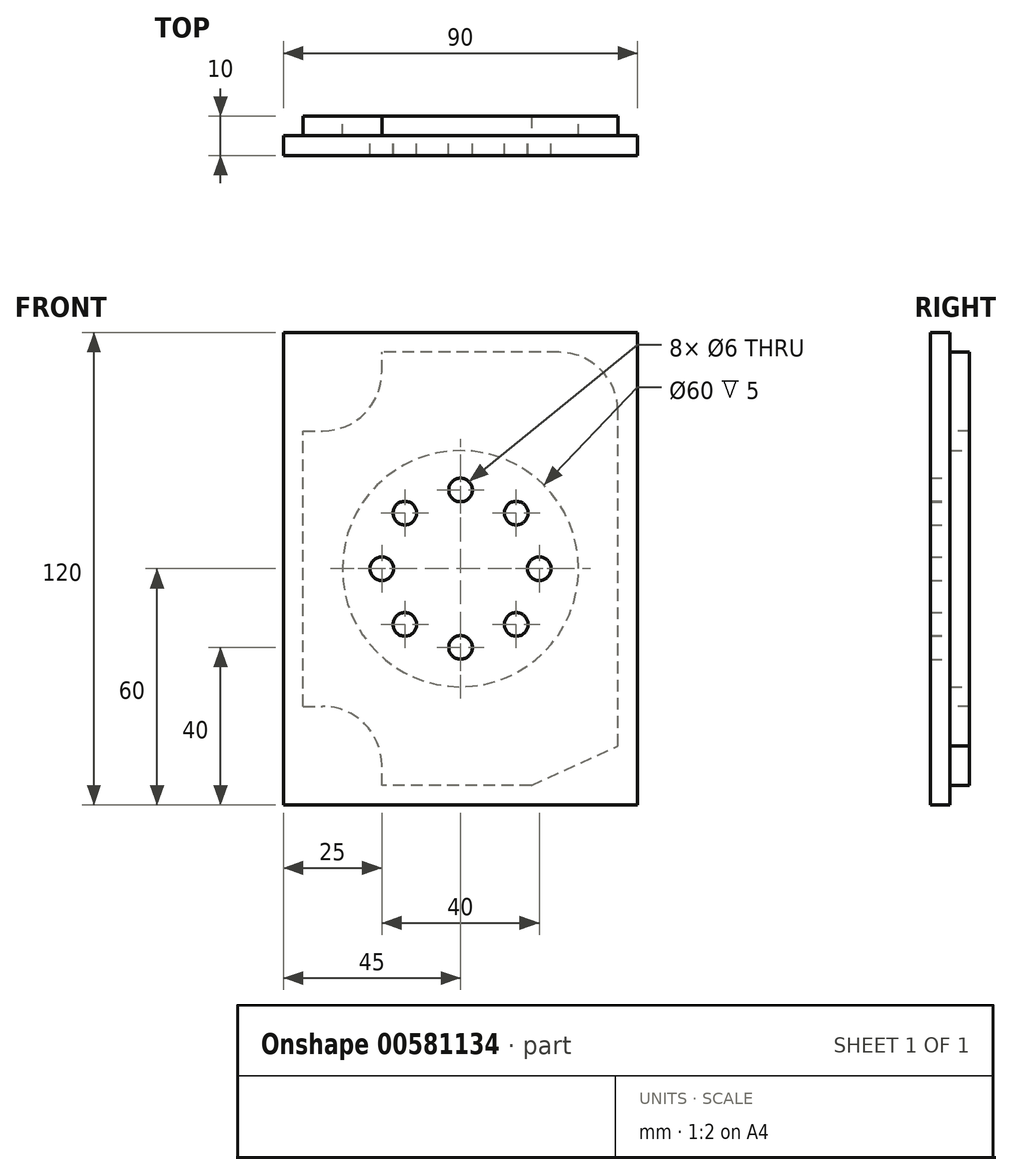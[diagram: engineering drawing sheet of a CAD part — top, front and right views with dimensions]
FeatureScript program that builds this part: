
annotation { "Feature Type Name" : "Feature", "Feature Type Description" : "" }
export const myFeature = defineFeature(function(context is Context, id is Id, definition is map)
    precondition{}
    {
        {
            var Q0;
            Q0=qCreatedBy(makeId("Front.planeOp"),FACE);
            var sketch = newSketch(context, id + "F0", { "sketchPlane" : qUnion([Q0])});
            skLineSegment(sketch, "E0.bottom", {"start": v(45, -60) * mm, "end": v(-45, -60) * mm});
            skLineSegment(sketch, "E0.top", {"start": v(45, 60) * mm, "end": v(-45, 60) * mm});
            skLineSegment(sketch, "E0.left", {"start": v(45, -60) * mm, "end": v(45, 60) * mm});
            skLineSegment(sketch, "E0.right", {"start": v(-45, -60) * mm, "end": v(-45, 60) * mm});
            skLineSegment(sketch, "E1", {"start": v(0, -60) * mm, "end": v(0, 0) * mm, "construction": true});
            skLineSegment(sketch, "E2", {"start": v(0, 0) * mm, "end": v(45, 0) * mm, "construction": true});
            skSolve(sketch);
        }
        {
            var Q0;
            Q0=makeQuery(id+"F0.imprint","IMPRINT",FACE,{"disambiguationData":[TD([[makeQuery(id+"F0.imprint","IMPRINT",EDGE,{"derivedFrom":sQuery(id+"F0.wireOp",EDGE,"E0.bottom")}),-1.0]])]});
            extrude(context, id + "F1", {"entities" : qUnion([Q0]), "depth" : 5 * mm, "offsetDistance" : 25 * mm});
        }
        {
            var Q0;
            Q0=makeQuery(id+"F1.opExtrude","CAP_FACE",FACE,{"disambiguationData":[OSD([sQuery(id+"F0.wireOp",EDGE,"E0.bottom"),sQuery(id+"F0.wireOp",EDGE,"E0.top"),sQuery(id+"F0.wireOp",EDGE,"E0.left"),sQuery(id+"F0.wireOp",EDGE,"E0.right")])],"isStart":true});
            var sketch = newSketch(context, id + "F2", { "sketchPlane" : qUnion([Q0])});
            skLineSegment(sketch, "E3.bottom", {"start": v(-18, -55) * mm, "end": v(20, -55) * mm});
            skLineSegment(sketch, "E3.top", {"start": v(-25, 55) * mm, "end": v(20, 55) * mm});
            skLineSegment(sketch, "E3.left", {"start": v(-40, -45) * mm, "end": v(-40, 40) * mm});
            skLineSegment(sketch, "E3.right", {"start": v(40, -35) * mm, "end": v(40, 35) * mm});
            skPoint(sketch, "E4.visualSharp", {"position": v(-40, 55) * mm});
            skArc(sketch, "E4.filletArc", {"start": v(-25, 55) * mm, "mid": v(-35.6, 50.6) * mm, "end": v(-40, 40) * mm});
            skLineSegment(sketch, "E5", {"start": v(-18, -55) * mm, "end": v(-40, -45) * mm});
            skLineSegment(sketch, "E6", {"start": v(20, -55) * mm, "end": v(20, -50) * mm});
            skLineSegment(sketch, "E7", {"start": v(40, -35) * mm, "end": v(35, -35) * mm});
            skLineSegment(sketch, "E8", {"start": v(40, 35) * mm, "end": v(35, 35) * mm});
            skLineSegment(sketch, "E9", {"start": v(20, 50) * mm, "end": v(20, 55) * mm});
            skArc(sketch, "E10", {"start": v(35, -35) * mm, "mid": v(24.4, -39.4) * mm, "end": v(20, -50) * mm});
            skPoint(sketch, "E11.visualSharp", {"position": v(20, 35) * mm});
            skArc(sketch, "E11.filletArc", {"start": v(20, 50) * mm, "mid": v(24.4, 39.4) * mm, "end": v(35, 35) * mm});
            skSolve(sketch);
        }
        {
            var Q0;
            Q0=makeQuery(id+"F2.imprint","IMPRINT",FACE,{"disambiguationData":[TD([[makeQuery(id+"F2.imprint","IMPRINT",EDGE,{"derivedFrom":sQuery(id+"F2.wireOp",EDGE,"E3.bottom")}),1.0]])]});
            extrude(context, id + "F3", {"entities" : qUnion([Q0]), "operationType" : NewBodyOperationType.ADD, "depth" : 5 * mm, "offsetDistance" : 25 * mm});
        }
        {
            var Q0;
            Q0=makeQuery(id+"F3.opExtrude","CAP_FACE",FACE,{"disambiguationData":[OSD([sQuery(id+"F2.wireOp",EDGE,"E3.bottom"),sQuery(id+"F2.wireOp",EDGE,"E3.top"),sQuery(id+"F2.wireOp",EDGE,"E3.left"),sQuery(id+"F2.wireOp",EDGE,"E3.right"),sQuery(id+"F2.wireOp",EDGE,"E4.filletArc"),sQuery(id+"F2.wireOp",EDGE,"E5"),sQuery(id+"F2.wireOp",EDGE,"E6"),sQuery(id+"F2.wireOp",EDGE,"E7"),sQuery(id+"F2.wireOp",EDGE,"E8"),sQuery(id+"F2.wireOp",EDGE,"E9"),sQuery(id+"F2.wireOp",EDGE,"E10"),sQuery(id+"F2.wireOp",EDGE,"E11.filletArc")])],"isStart":false});
            var sketch = newSketch(context, id + "F4", { "sketchPlane" : qUnion([Q0])});
            skCircle(sketch, "E12", {"center": v(0, 0) * mm, "radius": 30 * mm});
            skCircle(sketch, "E13", {"center": v(0, 0) * mm, "radius": 20 * mm, "construction": true});
            skLineSegment(sketch, "E14", {"start": v(0, -55) * mm, "end": v(0, 55) * mm, "construction": true});
            skLineSegment(sketch, "E15", {"start": v(-40, 0) * mm, "end": v(40, 0) * mm, "construction": true});
            skCircle(sketch, "E16", {"center": v(0, -20) * mm, "radius": 3 * mm});
            skCircle(sketch, "E17", {"center": v(0, 20) * mm, "radius": 3 * mm});
            skCircle(sketch, "E18", {"center": v(-20, 0) * mm, "radius": 3 * mm});
            skCircle(sketch, "E19", {"center": v(20, 0) * mm, "radius": 3 * mm});
            skCircle(sketch, "E20", {"center": v(-14.14, -14.14) * mm, "radius": 3 * mm});
            skCircle(sketch, "E21", {"center": v(-14.14, 14.14) * mm, "radius": 3 * mm});
            skCircle(sketch, "E22", {"center": v(14.14, -14.14) * mm, "radius": 3 * mm});
            skCircle(sketch, "E23", {"center": v(14.14, 14.14) * mm, "radius": 3 * mm});
            skSolve(sketch);
        }
        {
            var Q0;
            Q0=makeQuery(id+"F4.imprint","IMPRINT",FACE,{"disambiguationData":[TD([[makeQuery(id+"F4.imprint","IMPRINT",EDGE,{"derivedFrom":sQuery(id+"F4.wireOp",EDGE,"E12")}),1.0]])]});
            extrude(context, id + "F5", {"entities" : qUnion([Q0]), "operationType" : NewBodyOperationType.REMOVE, "oppositeDirection" : true, "depth" : 5 * mm, "offsetDistance" : 25 * mm});
        }
        {
            var Q0;
            Q0=makeQuery(id+"F4.imprint","IMPRINT",FACE,{"disambiguationData":[TD([[makeQuery(id+"F4.imprint","IMPRINT",EDGE,{"derivedFrom":sQuery(id+"F4.wireOp",EDGE,"E20")}),1.0]])]});
            var Q1;
            Q1=makeQuery(id+"F4.imprint","IMPRINT",FACE,{"disambiguationData":[TD([[makeQuery(id+"F4.imprint","IMPRINT",EDGE,{"derivedFrom":sQuery(id+"F4.wireOp",EDGE,"E18")}),1.0]])]});
            var Q2;
            Q2=makeQuery(id+"F4.imprint","IMPRINT",FACE,{"disambiguationData":[TD([[makeQuery(id+"F4.imprint","IMPRINT",EDGE,{"derivedFrom":sQuery(id+"F4.wireOp",EDGE,"E21")}),1.0]])]});
            var Q3;
            Q3=makeQuery(id+"F4.imprint","IMPRINT",FACE,{"disambiguationData":[TD([[makeQuery(id+"F4.imprint","IMPRINT",EDGE,{"derivedFrom":sQuery(id+"F4.wireOp",EDGE,"E17")}),1.0]])]});
            var Q4;
            Q4=makeQuery(id+"F4.imprint","IMPRINT",FACE,{"disambiguationData":[TD([[makeQuery(id+"F4.imprint","IMPRINT",EDGE,{"derivedFrom":sQuery(id+"F4.wireOp",EDGE,"E23")}),1.0]])]});
            var Q5;
            Q5=makeQuery(id+"F4.imprint","IMPRINT",FACE,{"disambiguationData":[TD([[makeQuery(id+"F4.imprint","IMPRINT",EDGE,{"derivedFrom":sQuery(id+"F4.wireOp",EDGE,"E19")}),1.0]])]});
            var Q6;
            Q6=makeQuery(id+"F4.imprint","IMPRINT",FACE,{"disambiguationData":[TD([[makeQuery(id+"F4.imprint","IMPRINT",EDGE,{"derivedFrom":sQuery(id+"F4.wireOp",EDGE,"E22")}),1.0]])]});
            var Q7;
            Q7=makeQuery(id+"F4.imprint","IMPRINT",FACE,{"disambiguationData":[TD([[makeQuery(id+"F4.imprint","IMPRINT",EDGE,{"derivedFrom":sQuery(id+"F4.wireOp",EDGE,"E16")}),1.0]])]});
            extrude(context, id + "F6", {"entities" : qUnion([Q0, Q1, Q2, Q3, Q4, Q5, Q6, Q7]), "operationType" : NewBodyOperationType.REMOVE, "oppositeDirection" : true, "depth" : 25 * mm, "offsetDistance" : 25 * mm});
        }
    });
